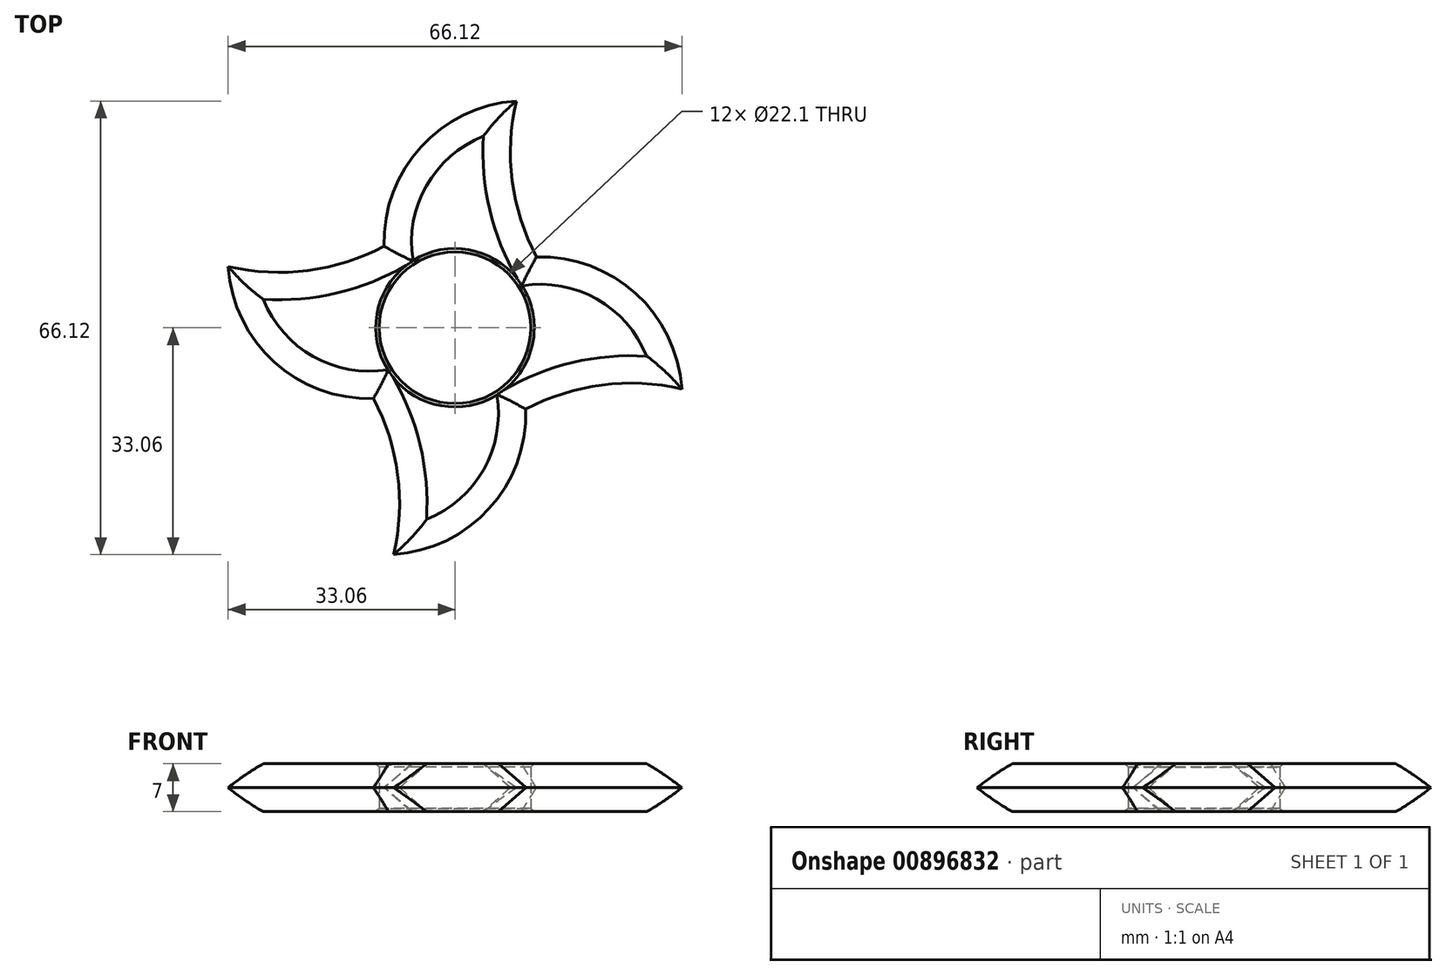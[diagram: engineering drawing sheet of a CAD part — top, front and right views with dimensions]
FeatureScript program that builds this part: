
annotation { "Feature Type Name" : "Feature", "Feature Type Description" : "" }
export const myFeature = defineFeature(function(context is Context, id is Id, definition is map)
    precondition{}
    {
        {
            var Q0;
            Q0=qCreatedBy(makeId("Top.planeOp"),FACE);
            var sketch = newSketch(context, id + "F0", { "sketchPlane" : qUnion([Q0])});
            skCircle(sketch, "E0", {"center": v(0, 0) * mm, "radius": 11.05 * mm});
            skArc(sketch, "E1", {"start": v(8.93, 33.06) * mm, "mid": v(-4.97, 26.36) * mm, "end": v(-10.32, 11.88) * mm});
            skArc(sketch, "E2.1.0", {"start": v(-33.06, 8.93) * mm, "mid": v(-26.36, -4.97) * mm, "end": v(-11.88, -10.32) * mm});
            skArc(sketch, "E2.2.0", {"start": v(-8.93, -33.06) * mm, "mid": v(4.97, -26.36) * mm, "end": v(10.32, -11.88) * mm});
            skArc(sketch, "E2.3.0", {"start": v(33.06, -8.93) * mm, "mid": v(26.36, 4.97) * mm, "end": v(11.88, 10.32) * mm});
            skArc(sketch, "E3", {"start": v(8.93, 33.06) * mm, "mid": v(8.35, 21.42) * mm, "end": v(11.88, 10.32) * mm});
            skArc(sketch, "E4.1.0", {"start": v(-33.06, 8.93) * mm, "mid": v(-21.42, 8.35) * mm, "end": v(-10.32, 11.88) * mm});
            skArc(sketch, "E4.2.0", {"start": v(-8.93, -33.06) * mm, "mid": v(-8.35, -21.42) * mm, "end": v(-11.88, -10.32) * mm});
            skArc(sketch, "E4.3.0", {"start": v(33.06, -8.93) * mm, "mid": v(21.42, -8.35) * mm, "end": v(10.32, -11.88) * mm});
            skSolve(sketch);
        }
        {
            var Q0;
            Q0=makeQuery(id+"F0.imprint","IMPRINT",FACE,{"disambiguationData":[TD([[makeQuery(id+"F0.imprint","IMPRINT",EDGE,{"derivedFrom":sQuery(id+"F0.wireOp",EDGE,"E0")}),-1.0]])]});
            extrude(context, id + "F1", {"entities" : qUnion([Q0]), "endBound" : BoundingType.SYMMETRIC, "depth" : 7 * mm, "offsetDistance" : 25 * mm});
        }
        {
            var Q0;
            Q0=makeQuery(id+"F1.opExtrude","CAP_EDGE",EDGE,{"disambiguationData":[OSD([sQuery(id+"F0.wireOp",EDGE,"E4.1.0")])],"isStart":false});
            var Q1;
            Q1=makeQuery(id+"F1.opExtrude","CAP_EDGE",EDGE,{"disambiguationData":[OSD([sQuery(id+"F0.wireOp",EDGE,"E2.1.0")])],"isStart":false});
            var Q2;
            Q2=makeQuery(id+"F1.opExtrude","CAP_EDGE",EDGE,{"disambiguationData":[OSD([sQuery(id+"F0.wireOp",EDGE,"E4.2.0")])],"isStart":false});
            var Q3;
            Q3=makeQuery(id+"F1.opExtrude","CAP_EDGE",EDGE,{"disambiguationData":[OSD([sQuery(id+"F0.wireOp",EDGE,"E2.2.0")])],"isStart":false});
            var Q4;
            Q4=makeQuery(id+"F1.opExtrude","CAP_EDGE",EDGE,{"disambiguationData":[OSD([sQuery(id+"F0.wireOp",EDGE,"E4.3.0")])],"isStart":false});
            var Q5;
            Q5=makeQuery(id+"F1.opExtrude","CAP_EDGE",EDGE,{"disambiguationData":[OSD([sQuery(id+"F0.wireOp",EDGE,"E2.3.0")])],"isStart":false});
            var Q6;
            Q6=makeQuery(id+"F1.opExtrude","CAP_EDGE",EDGE,{"disambiguationData":[OSD([sQuery(id+"F0.wireOp",EDGE,"E3")])],"isStart":false});
            var Q7;
            Q7=makeQuery(id+"F1.opExtrude","CAP_EDGE",EDGE,{"disambiguationData":[OSD([sQuery(id+"F0.wireOp",EDGE,"E1")])],"isStart":false});
            chamfer(context, id + "F2", {"entities" : qUnion([Q0, Q1, Q2, Q3, Q4, Q5, Q6, Q7]), "chamferType" : ChamferType.TWO_OFFSETS, "width1" : 3.5 * mm, "oppositeDirection" : false, "width2" : 4 * mm, "tangentPropagation" : true});
        }
        {
            var Q0;
            Q0=makeQuery(id+"F1.opExtrude","CAP_EDGE",EDGE,{"disambiguationData":[OSD([sQuery(id+"F0.wireOp",EDGE,"E2.3.0")])],"isStart":true});
            var Q1;
            Q1=makeQuery(id+"F1.opExtrude","CAP_EDGE",EDGE,{"disambiguationData":[OSD([sQuery(id+"F0.wireOp",EDGE,"E3")])],"isStart":true});
            var Q2;
            Q2=makeQuery(id+"F1.opExtrude","CAP_EDGE",EDGE,{"disambiguationData":[OSD([sQuery(id+"F0.wireOp",EDGE,"E1")])],"isStart":true});
            var Q3;
            Q3=makeQuery(id+"F1.opExtrude","CAP_EDGE",EDGE,{"disambiguationData":[OSD([sQuery(id+"F0.wireOp",EDGE,"E4.1.0")])],"isStart":true});
            var Q4;
            Q4=makeQuery(id+"F1.opExtrude","CAP_EDGE",EDGE,{"disambiguationData":[OSD([sQuery(id+"F0.wireOp",EDGE,"E2.1.0")])],"isStart":true});
            var Q5;
            Q5=makeQuery(id+"F1.opExtrude","CAP_EDGE",EDGE,{"disambiguationData":[OSD([sQuery(id+"F0.wireOp",EDGE,"E4.2.0")])],"isStart":true});
            var Q6;
            Q6=makeQuery(id+"F1.opExtrude","CAP_EDGE",EDGE,{"disambiguationData":[OSD([sQuery(id+"F0.wireOp",EDGE,"E2.2.0")])],"isStart":true});
            var Q7;
            Q7=makeQuery(id+"F1.opExtrude","CAP_EDGE",EDGE,{"disambiguationData":[OSD([sQuery(id+"F0.wireOp",EDGE,"E4.3.0")])],"isStart":true});
            chamfer(context, id + "F3", {"entities" : qUnion([Q0, Q1, Q2, Q3, Q4, Q5, Q6, Q7]), "chamferType" : ChamferType.TWO_OFFSETS, "width1" : 4 * mm, "oppositeDirection" : true, "width2" : 3.5 * mm, "tangentPropagation" : true});
        }
        {
            var Q0;
            Q0=makeQuery(id+"F1.opExtrude","SWEPT_FACE",FACE,{"disambiguationData":[OSD([sQuery(id+"F0.wireOp",EDGE,"E0")])]});
            chamfer(context, id + "F4", {"entities" : qUnion([Q0]), "width" : 0.5 * mm, "tangentPropagation" : true});
        }
    });
